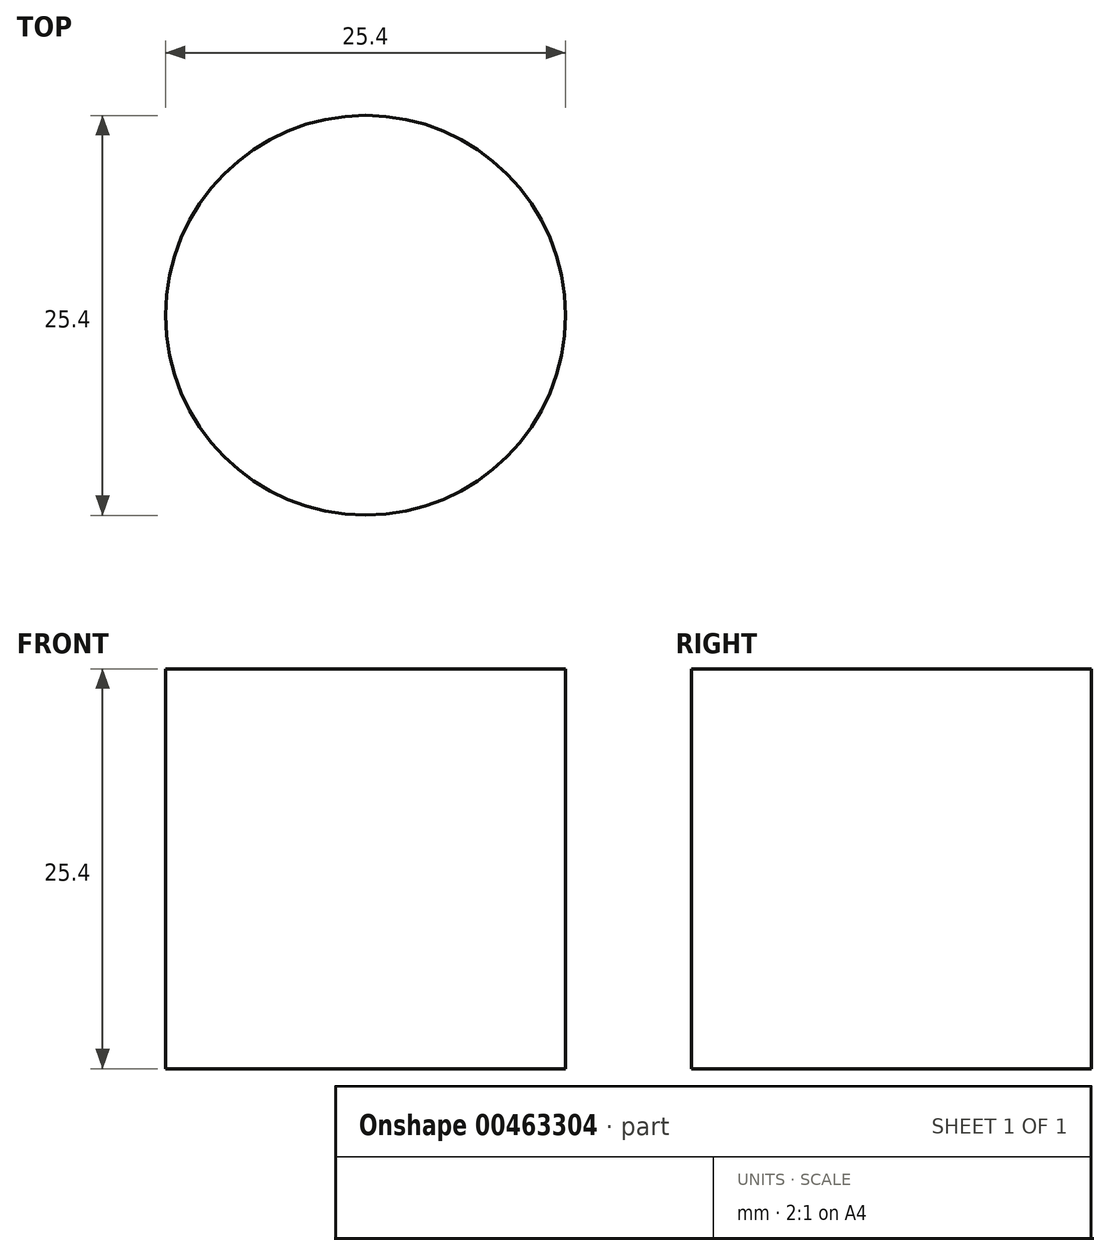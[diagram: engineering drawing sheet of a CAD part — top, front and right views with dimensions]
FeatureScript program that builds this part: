
annotation { "Feature Type Name" : "Feature", "Feature Type Description" : "" }
export const myFeature = defineFeature(function(context is Context, id is Id, definition is map)
    precondition{}
    {
        {
            var Q0;
            Q0=qCreatedBy(makeId("Top.planeOp"),FACE);
            var sketch = newSketch(context, id + "F0", { "sketchPlane" : qUnion([Q0])});
            skCircle(sketch, "E0", {"center": v(-15.42, 8.64) * mm, "radius": 12.7 * mm});
            skSolve(sketch);
        }
        {
            var Q0;
            Q0=makeQuery(id+"F0.imprint","IMPRINT",FACE,{"disambiguationData":[TD([[makeQuery(id+"F0.imprint","IMPRINT",EDGE,{"derivedFrom":sQuery(id+"F0.wireOp",EDGE,"E0")}),1.0]])]});
            extrude(context, id + "F1", {"entities" : qUnion([Q0]), "depth" : 25.4 * mm});
        }
    });
